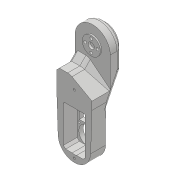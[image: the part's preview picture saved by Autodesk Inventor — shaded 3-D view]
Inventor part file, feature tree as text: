
AUTODESK INVENTOR PART (.ipt)
format: ipt  version: 2018 (Build 220112000, 112)  size: 979,456 bytes
history: native  units: mm
features: projected_geometry x42, sketch x41, extrude x34, fillet x13, chamfer x11, hole x8, other x4, mirror x1, reference x1
ambient origin geometry x8: Origin, YZ Plane, XZ Plane, XY Plane, X Axis, Y Axis, Z Axis, Center Point
bodies: Solid1 (feature_tree)
feature tree (155):
  extrude  "Extrusion1"  Depth=45.0mm
  extrude  "Extrusion2"  Depth=2.25mm
  hole  "Hole1"  [1 undecoded]
  hole  "Hole2"  [1 undecoded]
  fillet  "Fillet1"  Radius=14.0mm
  extrude  "Extrusion3"  Depth=18.5mm
  extrude  "Extrusion4"  Depth=10.0mm
  extrude  "Extrusion5"  Depth=2.195mm
  extrude  "Extrusion6"  Depth=20.5mm
  hole  "Hole3"  [1 undecoded]
  extrude  "Extrusion7"  Depth=0.5mm
  extrude  "Extrusion8"  Depth=5.0mm TaperAngle=0.0deg
  extrude  "Extrusion9"  Depth=10.0mm
  extrude  "Extrusion10"  Depth=10.0mm
  extrude  "Extrusion11"  Depth=14.5mm
  extrude  "Extrusion12"  Depth=14.5mm
  extrude  "Extrusion13"  Depth=5.0mm
  extrude  "Extrusion14"  Depth=5.0mm
  extrude  "Extrusion15"  Depth=5.0mm
  extrude  "Extrusion16"  Depth=5.0mm
  extrude  "Extrusion17"  Depth=4.0mm
  chamfer  "Chamfer1"  Distance=1.0mm
  fillet  "Fillet7"  Radius=20.7mm
  fillet  "Fillet8"  Radius=32.0mm
  mirror  "Mirror1"
  extrude  "Extrusion19"  Depth=5.0mm TaperAngle=0.0deg
  extrude  "Extrusion20"  Depth=8.0mm
  extrude  "Extrusion21"  Depth=0.2mm TaperAngle=0.0deg
  extrude  "Extrusion22"  Depth=0.5mm TaperAngle=0.0deg
  extrude  "Extrusion23"  Depth=9.0mm TaperAngle=0.0deg
  extrude  "Extrusion24"  Depth=5.0mm TaperAngle=0.0deg
  chamfer  "Chamfer2"  Distance=0.2mm
  chamfer  "Chamfer8"  Distance=2.5mm Angle=45.0deg
  extrude  "Extrusion25"  Depth=0.5mm
  extrude  "Extrusion26"  Depth=2.0mm TaperAngle=0.0deg
  chamfer  "Chamfer3"  Distance=2.0mm
  chamfer  "Chamfer4"  Distance=2.0mm
  chamfer  "Chamfer5"  Distance=15.0mm
  chamfer  "Chamfer6"  Distance=56.1mm
  fillet  "Fillet9"  Radius=41.6mm
  fillet  "Fillet10"  Radius=41.0mm
  hole  "Hole6"  [1 undecoded]
  fillet  "Fillet12"  Radius=7.0mm
  hole  "Hole7"  [1 undecoded]
  extrude  "Extrusion27"  Depth=3.0mm TaperAngle=45.0deg
  extrude  "Extrusion28"  Depth=5.0mm TaperAngle=45.0deg
  hole  "Hole8"  [1 undecoded]
  extrude  "Extrusion29"  Depth=10.0mm
  chamfer  "Chamfer7"  Distance=20.5mm
  fillet  "Fillet13"  Radius=1.6mm
  extrude  "Extrusion30"  Depth=10.0mm
  extrude  "Extrusion31"  Depth=10.0mm TaperAngle=0.0deg
  fillet  "Fillet14"  Radius=14.0mm
  extrude  "Extrusion32"  Depth=10.0mm
  fillet  "Fillet15"  Radius=3.1mm
  fillet  "Fillet18"  Radius=1.5mm
  extrude  "Extrusion35"  Depth=10.0mm
  extrude  "Extrusion36"  Depth=10.0mm
  chamfer  "Chamfer9"  Distance=10.0mm
  chamfer  "Chamfer10"  Distance=7.5mm
  chamfer  "Chamfer11"  Distance=6.0mm
  fillet  "Fillet19"  Radius=6.0mm
  hole  "Hole9"  [1 undecoded]
  fillet  "Fillet20"  Radius=6.0mm
  hole  "Hole10"  [1 undecoded]
  fillet  "Fillet21"  Radius=1.5mm
  extrude  "Extrusion37"  Depth=10.0mm
  sketch  "Sketch1"  dims[d0=24.5mm d1=45.0mm]
  sketch  "Sketch2"  dims[d2=1.95mm d3=0.0mm d4=2.25mm]
  projected_geometry  "Projected Loop1"
  sketch  "Sketch3"  dims[d5=20.0mm d6=2.25mm]
  projected_geometry  "Projected Loop2"
  sketch  "Sketch4"  dims[d7=5.25mm d8=5.25mm d9=14.0mm]
  projected_geometry  "Projected Loop3"
  sketch  "Sketch5"  dims[d10=5.25mm d11=18.5mm]
  projected_geometry  "Projected Loop4"
  sketch  "Sketch6"  dims[d12=10.0mm d13=0.0mm d14=20.5mm]
  projected_geometry  "Projected Loop5"
  sketch  "Sketch7"  dims[d15=2.0mm d16=2.195mm]
  projected_geometry  "Projected Loop6"
  sketch  "Sketch8"  dims[d17=2.0mm]
  projected_geometry  "Projected Loop7"
  sketch  "Sketch9"  dims[d18=2.4mm d19=6.0mm d20=4.4mm d21=2.0mm d22=90.0deg d23=8.0mm d24=20.594885mm d25=20.5mm]
  projected_geometry  "Projected Loop8"
  projected_geometry  "Projected Loop9"
  sketch  "Sketch10"  dims[d26=26.65mm d27=2.0mm]
  projected_geometry  "Projected Loop10"
  projected_geometry  "Projected Loop11"
  sketch  "Sketch11"  dims[d28=2.0mm]
  projected_geometry  "Projected Loop12"
  sketch  "Sketch12"  dims[d29=2.4mm d30=6.0mm d31=4.4mm d32=2.0mm d33=90.0deg d34=8.0mm d35=20.594885mm d36=0.5mm]
  sketch  "Sketch13"  dims[d37=18.0mm d38=5.0mm d39=0.0mm]
  sketch  "Sketch14"  dims[d41=10.0mm d42=0.0mm d43=24.5mm]
  projected_geometry  "Projected Loop13"
  sketch  "Sketch15"  dims[d44=1.15mm d45=0.0mm d46=10.0mm]
  sketch  "Sketch16"  dims[d47=21.0mm d48=14.5mm]
  projected_geometry  "Projected Loop14"
  sketch  "Sketch17"  dims[d49=20.0mm d50=14.5mm]
  projected_geometry  "Projected Loop15"
  sketch  "Sketch18"  dims[d51=24.5mm d52=5.0mm]
  projected_geometry  "Projected Loop16"
  sketch  "Sketch19"  dims[d53=5.0mm d54=2.25mm]
  projected_geometry  "Projected Loop17"
  sketch  "Sketch20"  dims[d55=2.25mm d56=5.0mm]
  projected_geometry  "Projected Loop18"
  sketch  "Sketch25"  dims[d57=5.0mm d58=9.0mm]
  projected_geometry  "Projected Loop22"
  sketch  "Sketch26"  dims[d59=14.75mm d60=4.0mm d61=1.0mm d62=0.0mm d63=20.7mm]
  projected_geometry  "Projected Loop23"
  sketch  "Sketch27"  dims[d64=2.4mm d65=6.0mm d66=4.4mm d67=2.0mm d68=90.0deg d69=8.0mm d70=20.594885mm d72=32.0mm]
  projected_geometry  "Projected Loop24"
  sketch  "Sketch28"  dims[d73=5.0mm d74=0.0mm d75=1.0mm d76=0.0mm]
  projected_geometry  "Projected Loop25"
  sketch  "Sketch29"  dims[d77=12.25mm d78=0.0mm d80=8.0mm]
  projected_geometry  "Projected Loop26"
  sketch  "Sketch30"  dims[d81=4.5mm d82=0.0mm d84=0.2mm d85=0.0mm]
  projected_geometry  "Projected Loop27"
  sketch  "Sketch31"  dims[d86=21.0mm d87=0.5mm d88=0.0mm]
  sketch  "Sketch33"  dims[d91=8.0mm d92=0.0mm d93=9.0mm d94=0.0mm]
  projected_geometry  "Projected Loop28"
  projected_geometry  "Projected Loop29"
  projected_geometry  "Projected Loop30"
  sketch  "Sketch34"  dims[d95=5.0mm d96=0.0mm d98=0.2mm d99=0.0mm d100=0.2mm d101=0.0mm d102=2.5mm d103=2.0mm d104=45.0deg]
  projected_geometry  "Projected Loop31"
  projected_geometry  "Projected Loop32"
  sketch  "Sketch35"  dims[d105=1.5mm d114=0.5mm]
  projected_geometry  "Projected Loop33"
  sketch  "Sketch36"  dims[d128=2.0mm d129=0.0mm d130=2.0mm d131=0.0mm]
  projected_geometry  "Projected Loop34"
  sketch  "Sketch37"  dims[d132=40.0mm d133=2.0mm d134=0.0mm d135=2.0mm d136=0.0mm]
  projected_geometry  "Projected Loop35"
  sketch  "Sketch38"  dims[d137=40.0mm]
  projected_geometry  "Projected Loop36"
  sketch  "Sketch39"  dims[d138=70.0mm d139=15.0mm d140=0.0mm d141=56.1mm d142=0.0mm]
  projected_geometry  "Projected Loop37"
  sketch  "Sketch40"  dims[d143=4.0mm d144=8.0mm d145=45.0deg d146=41.6mm d147=41.0mm]
  projected_geometry  "Projected Loop38"
  sketch  "Sketch41"  dims[d148=7.0mm d149=7.0mm d150=7.0mm]
  projected_geometry  "Projected Loop39"
  reference  "Reference1"
  sketch  "Sketch44"  dims[d151=100.0mm d152=0.0mm d153=15.282752mm]
  projected_geometry  "Projected Loop42"
  sketch  "Sketch45"  dims[d156=100.0mm d157=0.0mm d158=3.0mm d159=2.0mm d160=45.0deg]
  projected_geometry  "Projected Loop43"
  sketch  "Sketch46"  dims[d161=5.0mm d162=2.0mm d163=45.0deg d164=5.0mm d165=2.0mm d166=45.0deg]
  projected_geometry  "Projected Loop44"
  sketch  "Sketch47"  dims[d167=5.0mm d168=2.0mm d169=45.0deg d170=5.0mm]
  projected_geometry  "Projected Loop45"
  sketch  "Sketch48"  dims[d171=2.0mm d173=5.7mm d174=6.0mm d175=4.0mm d176=2.0mm d177=90.0deg d178=25.0mm d179=0.0mm d180=1.0mm d181=2.459mm d182=25.0mm d183=4.0mm d184=2.0mm d185=90.0deg d186=25.0mm d187=20.594885mm d188=20.5mm d189=1.6mm d190=0.0mm d191=20.5mm d192=3.1mm d193=0.0mm d194=14.0mm d195=3.2mm d196=25.0mm d197=6.3mm d198=2.0mm d199=90.0deg d200=25.0mm d201=20.594885mm d202=16.0mm d203=3.1mm d204=0.0mm d205=1.5mm d206=2.0mm d207=45.0deg d208=1.7mm d209=37.0mm d210=10.0mm d211=0.0mm d212=7.5mm d213=6.0mm d214=6.0mm d215=6.0mm d216=6.0mm d217=5.0mm d218=0.0mm d219=1.5mm d220=6.0mm d221=6.0mm d222=6.0mm d223=6.0mm d224=6.0mm d225=0.0mm d226=1.5mm d231=4.0mm d232=8.0mm d233=45.0deg d234=10.0mm d237=7.0mm d238=2.5mm d239=0.0mm d240=7.0mm d241=2.5mm d242=0.0mm d243=14.0mm d244=25.0mm d245=45.0deg d246=14.0mm d247=25.0mm d248=45.0deg d249=14.0mm d250=25.0mm d251=45.0deg d252=10.0mm d253=4.0mm d254=6.0mm d255=4.0mm d256=2.0mm d257=90.0deg d258=2.0mm d259=20.594885mm d260=1.0mm d261=4.0mm d262=6.0mm d263=4.0mm d264=2.0mm d265=90.0deg d266=2.0mm d267=20.594885mm d268=1.0mm d269=35.55mm d270=0.0mm]
  projected_geometry  "Project Cut Edges1"
  projected_geometry  "Project Cut Edges2"
  parser-record x1  (decoder bookkeeping rows leaked as tree rows — omitted from the tree; the rows remain in map.json)
  other  "servocheck.iam"
  other  "bottomarm:1"
  other  "arm1:1"
note: 8 required parameter values undecoded (feature->parameter linkage not recoverable at this tier; creation-order binding heuristic only, values carry confidence <= 0.55)
note: 1 file-system path scrubbed to <path> (originals preserved in map.json)
